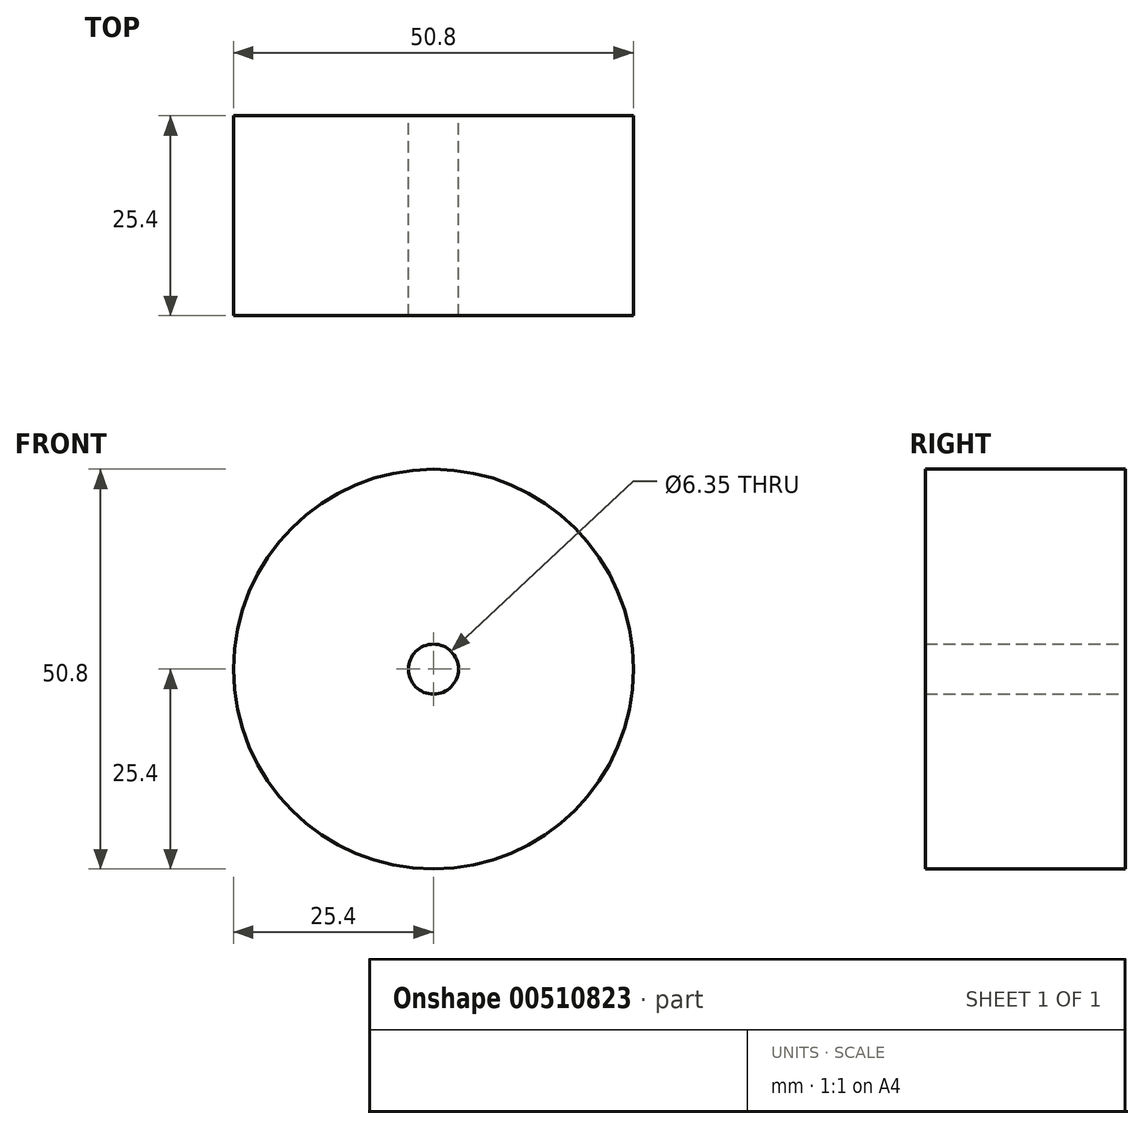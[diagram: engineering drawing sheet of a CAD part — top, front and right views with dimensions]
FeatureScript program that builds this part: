
annotation { "Feature Type Name" : "Feature", "Feature Type Description" : "" }
export const myFeature = defineFeature(function(context is Context, id is Id, definition is map)
    precondition{}
    {
        {
            var Q0;
            Q0=qCreatedBy(makeId("Front.planeOp"),FACE);
            var sketch = newSketch(context, id + "F0", { "sketchPlane" : qUnion([Q0])});
            skCircle(sketch, "E0", {"center": v(0, 0) * mm, "radius": 25.4 * mm});
            skCircle(sketch, "E1", {"center": v(0, 0) * mm, "radius": 3.18 * mm});
            skSolve(sketch);
        }
        {
            var Q0;
            Q0=makeQuery(id+"F0.imprint","IMPRINT",FACE,{"disambiguationData":[TD([[makeQuery(id+"F0.imprint","IMPRINT",EDGE,{"derivedFrom":sQuery(id+"F0.wireOp",EDGE,"E0")}),1.0]])]});
            extrude(context, id + "F1", {"entities" : qUnion([Q0]), "depth" : 25.4 * mm, "offsetDistance" : 25.4 * mm});
        }
    });
